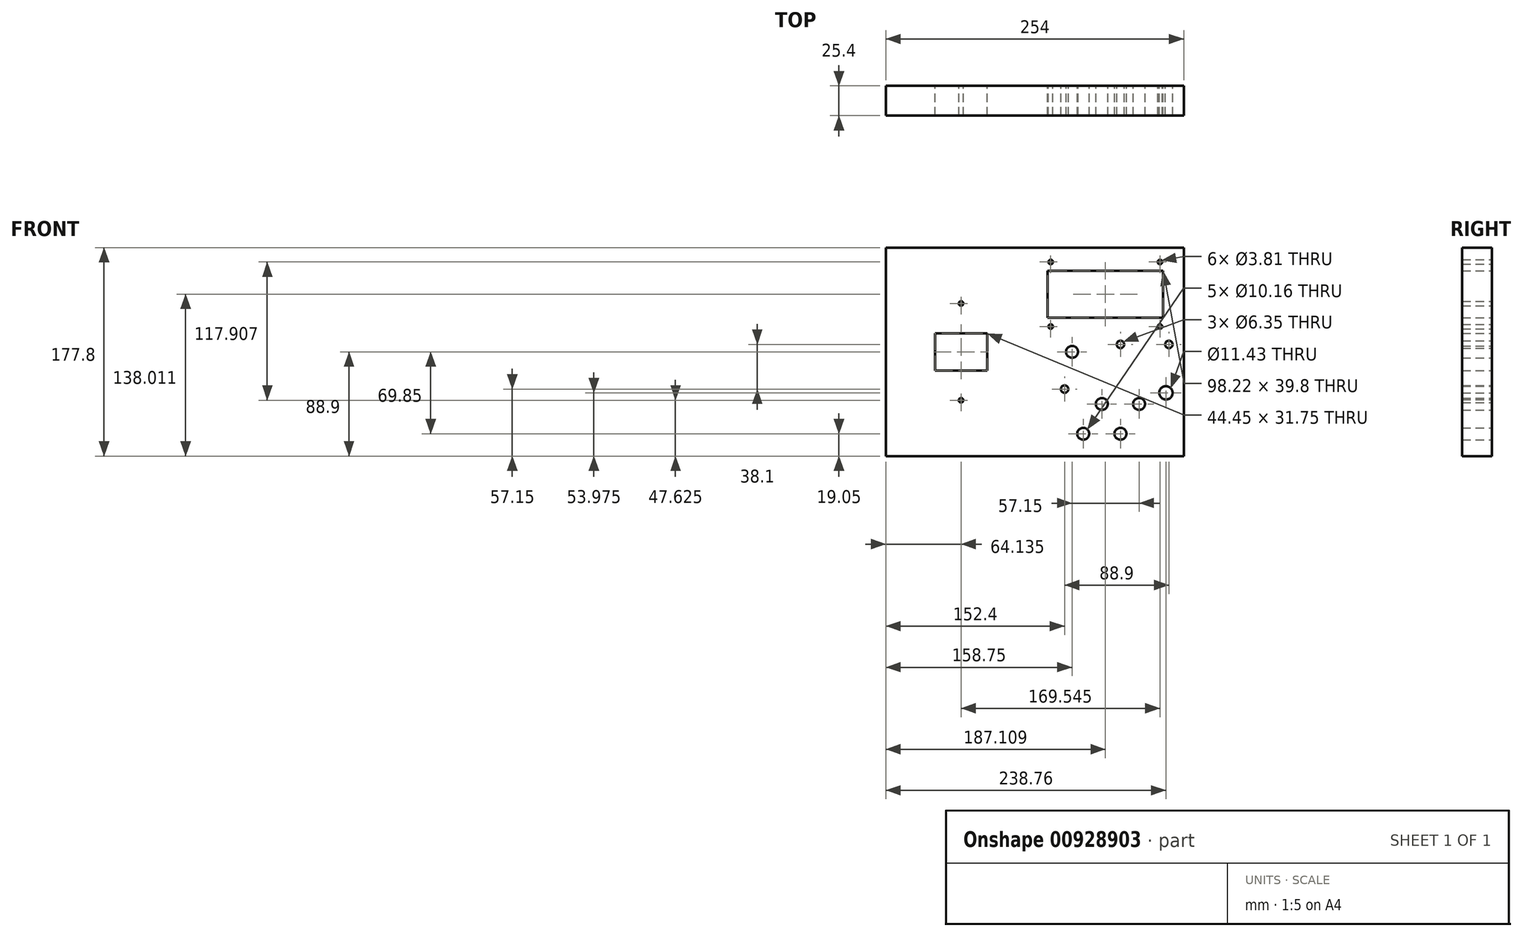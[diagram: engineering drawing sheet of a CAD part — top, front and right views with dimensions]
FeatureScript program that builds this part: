
annotation { "Feature Type Name" : "Feature", "Feature Type Description" : "" }
export const myFeature = defineFeature(function(context is Context, id is Id, definition is map)
    precondition{}
    {
        {
            var Q0;
            Q0=qCreatedBy(makeId("Front.planeOp"),FACE);
            var sketch = newSketch(context, id + "F0", { "sketchPlane" : qUnion([Q0])});
            skLineSegment(sketch, "E0.bottom", {"start": v(0, 0) * mm, "end": v(254, 0) * mm});
            skLineSegment(sketch, "E0.top", {"start": v(0, -177.8) * mm, "end": v(254, -177.8) * mm});
            skLineSegment(sketch, "E0.left", {"start": v(0, 0) * mm, "end": v(0, -177.8) * mm});
            skLineSegment(sketch, "E0.right", {"start": v(254, 0) * mm, "end": v(254, -177.8) * mm});
            skLineSegment(sketch, "E1.bottom", {"start": v(41.9, -73.02) * mm, "end": v(86.36, -73.02) * mm});
            skLineSegment(sketch, "E1.top", {"start": v(41.91, -104.77) * mm, "end": v(86.36, -104.77) * mm});
            skLineSegment(sketch, "E1.left", {"start": v(41.9, -73.02) * mm, "end": v(41.9, -104.77) * mm});
            skLineSegment(sketch, "E1.right", {"start": v(86.36, -73.02) * mm, "end": v(86.36, -104.77) * mm});
            skLineSegment(sketch, "E2", {"start": v(64.14, -130.17) * mm, "end": v(64.13, -47.62) * mm, "construction": true});
            skPoint(sketch, "E2.startSnap0", {"position": v(64.14, -104.77) * mm});
            skPoint(sketch, "E2.endSnap0", {"position": v(64.13, -73.02) * mm});
            skLineSegment(sketch, "E3", {"start": v(138, -19.89) * mm, "end": v(236.22, -19.89) * mm});
            skLineSegment(sketch, "E4", {"start": v(138, -59.69) * mm, "end": v(236.22, -59.69) * mm});
            skCircle(sketch, "E5", {"center": v(140.54, -67.3) * mm, "radius": 1.9 * mm});
            skCircle(sketch, "E6", {"center": v(140.54, -12.27) * mm, "radius": 1.9 * mm});
            skCircle(sketch, "E7", {"center": v(233.68, -12.27) * mm, "radius": 1.9 * mm});
            skCircle(sketch, "E8", {"center": v(233.68, -67.3) * mm, "radius": 1.9 * mm});
            skCircle(sketch, "E9", {"center": v(64.14, -130.17) * mm, "radius": 1.9 * mm});
            skCircle(sketch, "E10", {"center": v(64.13, -47.62) * mm, "radius": 1.9 * mm});
            skCircle(sketch, "E11", {"center": v(238.76, -123.82) * mm, "radius": 5.72 * mm});
            skCircle(sketch, "E12", {"center": v(200.03, -158.75) * mm, "radius": 5.08 * mm});
            skCircle(sketch, "E13", {"center": v(168.28, -158.75) * mm, "radius": 5.08 * mm});
            skCircle(sketch, "E14", {"center": v(184.15, -133.35) * mm, "radius": 5.08 * mm});
            skCircle(sketch, "E15", {"center": v(215.9, -133.35) * mm, "radius": 5.08 * mm});
            skCircle(sketch, "E16", {"center": v(158.75, -88.9) * mm, "radius": 5.08 * mm});
            skCircle(sketch, "E17", {"center": v(200.03, -82.55) * mm, "radius": 3.18 * mm});
            skCircle(sketch, "E18", {"center": v(241.3, -82.55) * mm, "radius": 3.18 * mm});
            skCircle(sketch, "E19", {"center": v(152.4, -120.65) * mm, "radius": 3.18 * mm});
            skLineSegment(sketch, "E20", {"start": v(138, -19.89) * mm, "end": v(138, -59.69) * mm});
            skLineSegment(sketch, "E21", {"start": v(236.22, -19.89) * mm, "end": v(236.22, -59.69) * mm});
            skLineSegment(sketch, "E22", {"start": v(184.15, -133.35) * mm, "end": v(215.9, -133.35) * mm, "construction": true});
            skLineSegment(sketch, "E23", {"start": v(168.28, -158.75) * mm, "end": v(200.03, -158.75) * mm, "construction": true});
            skLineSegment(sketch, "E24", {"start": v(140.54, -12.27) * mm, "end": v(140.54, -67.3) * mm, "construction": true});
            skLineSegment(sketch, "E25", {"start": v(140.54, -12.27) * mm, "end": v(233.68, -12.27) * mm, "construction": true});
            skLineSegment(sketch, "E26", {"start": v(233.68, -12.27) * mm, "end": v(233.68, -67.3) * mm, "construction": true});
            skLineSegment(sketch, "E27", {"start": v(233.68, -67.3) * mm, "end": v(140.54, -67.3) * mm, "construction": true});
            skLineSegment(sketch, "E28", {"start": v(200.03, -82.55) * mm, "end": v(241.3, -82.55) * mm, "construction": true});
            skSolve(sketch);
        }
        {
            var Q0;
            Q0 = qSketchRegion(id + "F0", true);
            extrude(context, id + "F1", {"entities" : qUnion([Q0]), "depth" : 25.4 * mm, "offsetDistance" : 25.4 * mm});
        }
    });
